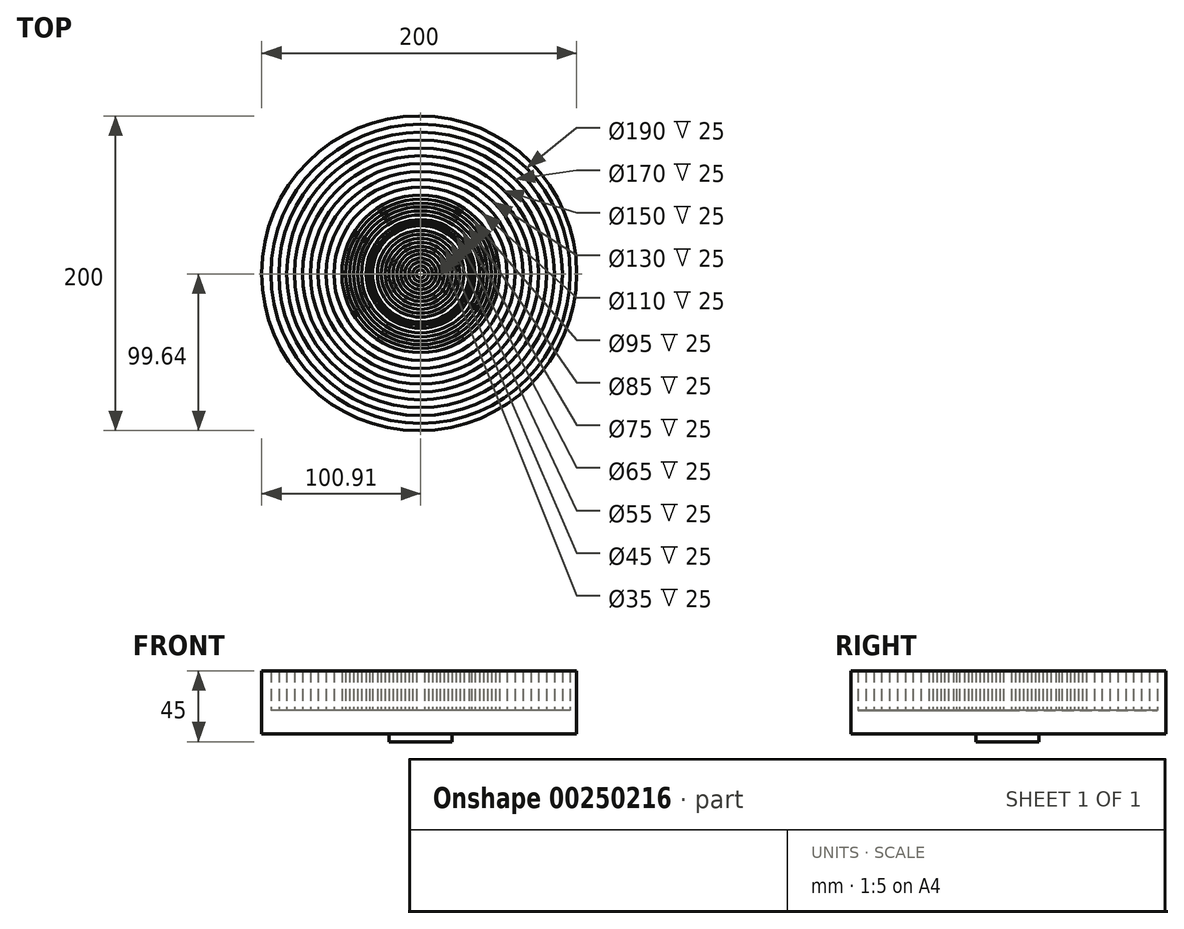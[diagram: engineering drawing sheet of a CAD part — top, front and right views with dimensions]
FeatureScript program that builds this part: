
annotation { "Feature Type Name" : "Feature", "Feature Type Description" : "" }
export const myFeature = defineFeature(function(context is Context, id is Id, definition is map)
    precondition{}
    {
        {
            var Q0;
            Q0=qCreatedBy(makeId("Top.planeOp"),FACE);
            var sketch = newSketch(context, id + "F0", { "sketchPlane" : qUnion([Q0])});
            skCircle(sketch, "E0", {"center": v(-0.9, 0.36) * mm, "radius": 100 * mm});
            skSolve(sketch);
        }
        {
            var Q0;
            Q0=makeQuery(id+"F0.imprint","IMPRINT",FACE,{"disambiguationData":[TD([[makeQuery(id+"F0.imprint","IMPRINT",EDGE,{"derivedFrom":sQuery(id+"F0.wireOp",EDGE,"E0")}),1.0]])]});
            extrude(context, id + "F1", {"entities" : qUnion([Q0]), "depth" : 15 * mm});
        }
        {
            var Q0;
            Q0=makeQuery(id+"F1.opExtrude","CAP_FACE",FACE,{"disambiguationData":[OSD([sQuery(id+"F0.wireOp",EDGE,"E0")])],"isStart":false});
            var sketch = newSketch(context, id + "F2", { "sketchPlane" : qUnion([Q0])});
            skCircle(sketch, "E1", {"center": v(0, 0) * mm, "radius": 95 * mm});
            skCircle(sketch, "E2", {"center": v(0, 0) * mm, "radius": 90 * mm});
            skCircle(sketch, "E3", {"center": v(0, 0) * mm, "radius": 85 * mm});
            skCircle(sketch, "E4", {"center": v(0, 0) * mm, "radius": 80 * mm});
            skCircle(sketch, "E5", {"center": v(0, 0) * mm, "radius": 75 * mm});
            skCircle(sketch, "E6", {"center": v(0, 0) * mm, "radius": 70 * mm});
            skCircle(sketch, "E7", {"center": v(0, 0) * mm, "radius": 65 * mm});
            skCircle(sketch, "E8", {"center": v(0, 0) * mm, "radius": 60 * mm});
            skCircle(sketch, "E9", {"center": v(0, 0) * mm, "radius": 55 * mm});
            skCircle(sketch, "E10", {"center": v(0, 0) * mm, "radius": 50 * mm});
            skCircle(sketch, "E11", {"center": v(0, 0) * mm, "radius": 47.5 * mm});
            skCircle(sketch, "E12", {"center": v(0, 0) * mm, "radius": 45 * mm});
            skCircle(sketch, "E13", {"center": v(0, 0) * mm, "radius": 42.5 * mm});
            skCircle(sketch, "E14", {"center": v(0, 0) * mm, "radius": 40 * mm});
            skCircle(sketch, "E15", {"center": v(0, 0) * mm, "radius": 37.5 * mm});
            skCircle(sketch, "E16", {"center": v(0, 0) * mm, "radius": 34.5 * mm});
            skCircle(sketch, "E17", {"center": v(0, 0) * mm, "radius": 32.5 * mm});
            skCircle(sketch, "E18", {"center": v(0, 0) * mm, "radius": 27.5 * mm});
            skCircle(sketch, "E19", {"center": v(0, 0) * mm, "radius": 25 * mm});
            skCircle(sketch, "E20", {"center": v(0, 0) * mm, "radius": 22.5 * mm});
            skCircle(sketch, "E21", {"center": v(0, 0) * mm, "radius": 20 * mm});
            skCircle(sketch, "E22", {"center": v(0, 0) * mm, "radius": 17.5 * mm});
            skCircle(sketch, "E23", {"center": v(0, 0) * mm, "radius": 15 * mm});
            skCircle(sketch, "E24", {"center": v(0, 0) * mm, "radius": 12.5 * mm});
            skCircle(sketch, "E25", {"center": v(0, 0) * mm, "radius": 10 * mm});
            skCircle(sketch, "E26", {"center": v(0, 0) * mm, "radius": 2.56 * mm});
            skCircle(sketch, "E27", {"center": v(0, 0) * mm, "radius": 5 * mm});
            skCircle(sketch, "E28", {"center": v(0, 0) * mm, "radius": 7.5 * mm});
            skCircle(sketch, "E29", {"center": v(0, 0) * mm, "radius": 30.64 * mm});
            skSolve(sketch);
        }
        {
            var Q0;
            Q0=makeQuery(id+"F2.imprint","IMPRINT",FACE,{"disambiguationData":[TD([[makeQuery(id+"F2.imprint","IMPRINT",EDGE,{"derivedFrom":sQuery(id+"F2.wireOp",EDGE,"E1")}),-1.0]])]});
            var Q1;
            Q1=makeQuery(id+"F2.imprint","IMPRINT",FACE,{"disambiguationData":[TD([[makeQuery(id+"F2.imprint","IMPRINT",EDGE,{"derivedFrom":sQuery(id+"F2.wireOp",EDGE,"E2")}),1.0]])]});
            var Q2;
            Q2=makeQuery(id+"F2.imprint","IMPRINT",FACE,{"disambiguationData":[TD([[makeQuery(id+"F2.imprint","IMPRINT",EDGE,{"derivedFrom":sQuery(id+"F2.wireOp",EDGE,"E4")}),1.0]])]});
            var Q3;
            Q3=makeQuery(id+"F2.imprint","IMPRINT",FACE,{"disambiguationData":[TD([[makeQuery(id+"F2.imprint","IMPRINT",EDGE,{"derivedFrom":sQuery(id+"F2.wireOp",EDGE,"E6")}),1.0]])]});
            var Q4;
            Q4=makeQuery(id+"F2.imprint","IMPRINT",FACE,{"disambiguationData":[TD([[makeQuery(id+"F2.imprint","IMPRINT",EDGE,{"derivedFrom":sQuery(id+"F2.wireOp",EDGE,"E8")}),1.0]])]});
            var Q5;
            Q5=makeQuery(id+"F2.imprint","IMPRINT",FACE,{"disambiguationData":[TD([[makeQuery(id+"F2.imprint","IMPRINT",EDGE,{"derivedFrom":sQuery(id+"F2.wireOp",EDGE,"E10")}),1.0]])]});
            var Q6;
            Q6=makeQuery(id+"F2.imprint","IMPRINT",FACE,{"disambiguationData":[TD([[makeQuery(id+"F2.imprint","IMPRINT",EDGE,{"derivedFrom":sQuery(id+"F2.wireOp",EDGE,"E12")}),1.0]])]});
            var Q7;
            Q7=makeQuery(id+"F2.imprint","IMPRINT",FACE,{"disambiguationData":[TD([[makeQuery(id+"F2.imprint","IMPRINT",EDGE,{"derivedFrom":sQuery(id+"F2.wireOp",EDGE,"E14")}),1.0]])]});
            var Q8;
            Q8=makeQuery(id+"F2.imprint","IMPRINT",FACE,{"disambiguationData":[TD([[makeQuery(id+"F2.imprint","IMPRINT",EDGE,{"derivedFrom":sQuery(id+"F2.wireOp",EDGE,"E16")}),1.0]])]});
            var Q9;
            Q9=makeQuery(id+"F2.imprint","IMPRINT",FACE,{"disambiguationData":[TD([[makeQuery(id+"F2.imprint","IMPRINT",EDGE,{"derivedFrom":sQuery(id+"F2.wireOp",EDGE,"E18")}),-1.0]])]});
            var Q10;
            Q10=makeQuery(id+"F2.imprint","IMPRINT",FACE,{"disambiguationData":[TD([[makeQuery(id+"F2.imprint","IMPRINT",EDGE,{"derivedFrom":sQuery(id+"F2.wireOp",EDGE,"E19")}),1.0]])]});
            var Q11;
            Q11=makeQuery(id+"F2.imprint","IMPRINT",FACE,{"disambiguationData":[TD([[makeQuery(id+"F2.imprint","IMPRINT",EDGE,{"derivedFrom":sQuery(id+"F2.wireOp",EDGE,"E21")}),1.0]])]});
            var Q12;
            Q12=makeQuery(id+"F2.imprint","IMPRINT",FACE,{"disambiguationData":[TD([[makeQuery(id+"F2.imprint","IMPRINT",EDGE,{"derivedFrom":sQuery(id+"F2.wireOp",EDGE,"E23")}),1.0]])]});
            var Q13;
            Q13=makeQuery(id+"F2.imprint","IMPRINT",FACE,{"disambiguationData":[TD([[makeQuery(id+"F2.imprint","IMPRINT",EDGE,{"derivedFrom":sQuery(id+"F2.wireOp",EDGE,"E25")}),1.0]])]});
            var Q14;
            Q14=makeQuery(id+"F2.imprint","IMPRINT",FACE,{"disambiguationData":[TD([[makeQuery(id+"F2.imprint","IMPRINT",EDGE,{"derivedFrom":sQuery(id+"F2.wireOp",EDGE,"E26")}),-1.0]])]});
            extrude(context, id + "F3", {"entities" : qUnion([Q0, Q1, Q2, Q3, Q4, Q5, Q6, Q7, Q8, Q9, Q10, Q11, Q12, Q13, Q14]), "operationType" : NewBodyOperationType.ADD, "depth" : 25 * mm});
        }
        {
            var Q0;
            Q0=makeQuery(id+"F1.opExtrude","CAP_FACE",FACE,{"disambiguationData":[OSD([sQuery(id+"F0.wireOp",EDGE,"E0")])],"isStart":true});
            var sketch = newSketch(context, id + "F4", { "sketchPlane" : qUnion([Q0])});
            skCircle(sketch, "E30", {"center": v(0, 0) * mm, "radius": 20 * mm});
            skSolve(sketch);
        }
        {
            var Q0;
            Q0=makeQuery(id+"F4.imprint","IMPRINT",FACE,{"disambiguationData":[TD([[makeQuery(id+"F4.imprint","IMPRINT",EDGE,{"derivedFrom":sQuery(id+"F4.wireOp",EDGE,"E30")}),1.0]])]});
            extrude(context, id + "F5", {"entities" : qUnion([Q0]), "operationType" : NewBodyOperationType.ADD, "depth" : 5 * mm});
        }
    });
